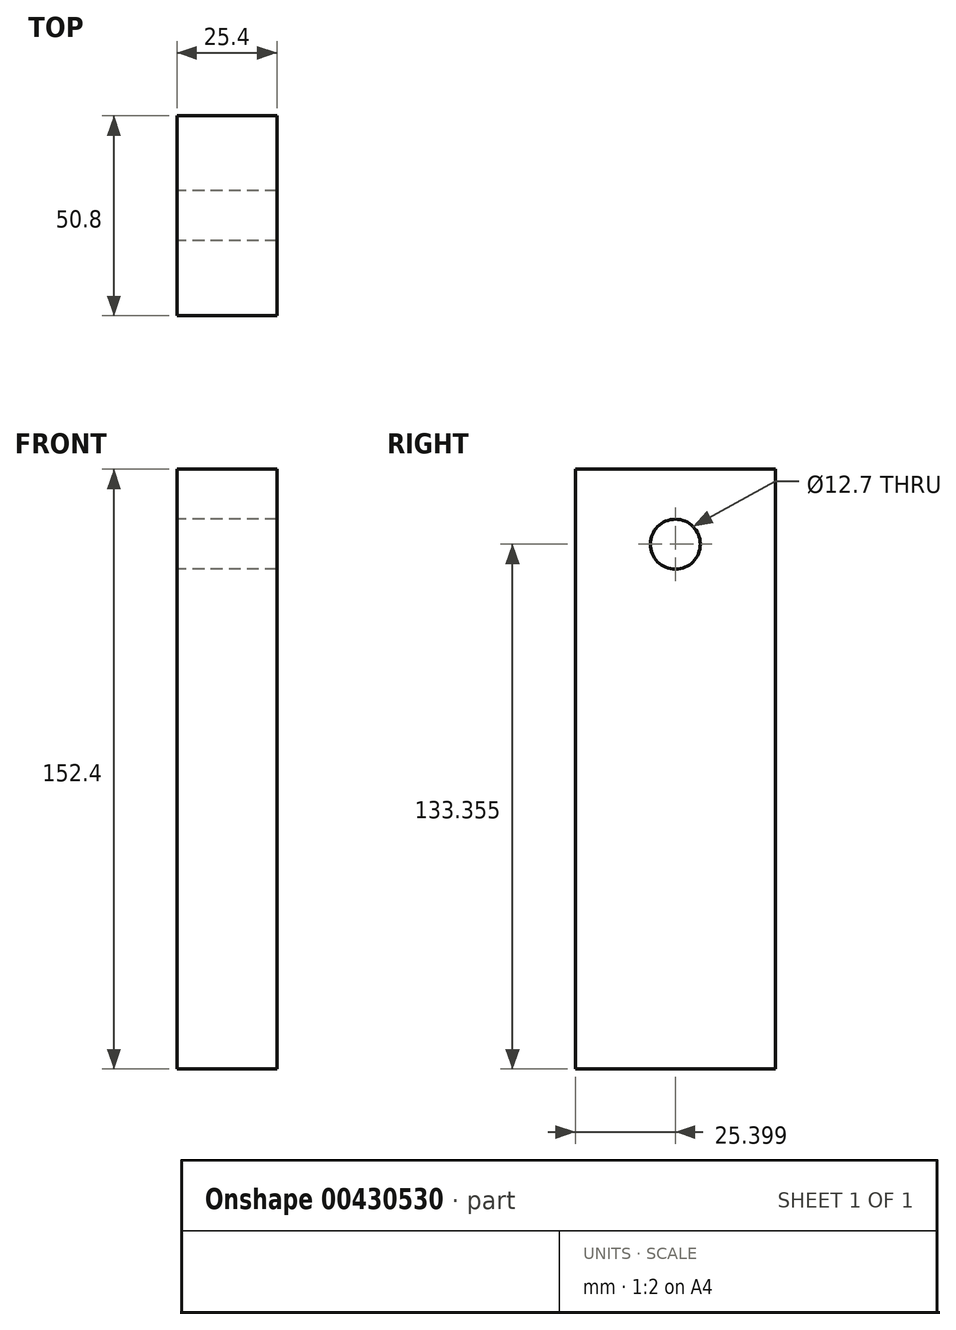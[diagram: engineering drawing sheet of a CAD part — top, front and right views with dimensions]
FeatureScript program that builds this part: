
annotation { "Feature Type Name" : "Feature", "Feature Type Description" : "" }
export const myFeature = defineFeature(function(context is Context, id is Id, definition is map)
    precondition{}
    {
        {
            var Q0;
            Q0=qCreatedBy(makeId("Right.planeOp"),FACE);
            var sketch = newSketch(context, id + "F0", { "sketchPlane" : qUnion([Q0])});
            skLineSegment(sketch, "E0.bottom", {"start": v(-55.82, 112.4) * mm, "end": v(-5.02, 112.4) * mm});
            skLineSegment(sketch, "E0.top", {"start": v(-55.82, -40) * mm, "end": v(-5.02, -40) * mm});
            skLineSegment(sketch, "E0.left", {"start": v(-55.82, 112.4) * mm, "end": v(-55.82, -40) * mm});
            skLineSegment(sketch, "E0.right", {"start": v(-5.02, 112.4) * mm, "end": v(-5.02, -40) * mm});
            skCircle(sketch, "E1", {"center": v(-30.42, 93.34) * mm, "radius": 6.35 * mm});
            skSolve(sketch);
        }
        {
            var Q0;
            Q0=makeQuery(id+"F0.imprint","IMPRINT",FACE,{"disambiguationData":[TD([[makeQuery(id+"F0.imprint","IMPRINT",EDGE,{"derivedFrom":sQuery(id+"F0.wireOp",EDGE,"E0.bottom")}),-1.0]])]});
            extrude(context, id + "F1", {"entities" : qUnion([Q0]), "depth" : 25.4 * mm});
        }
    });
